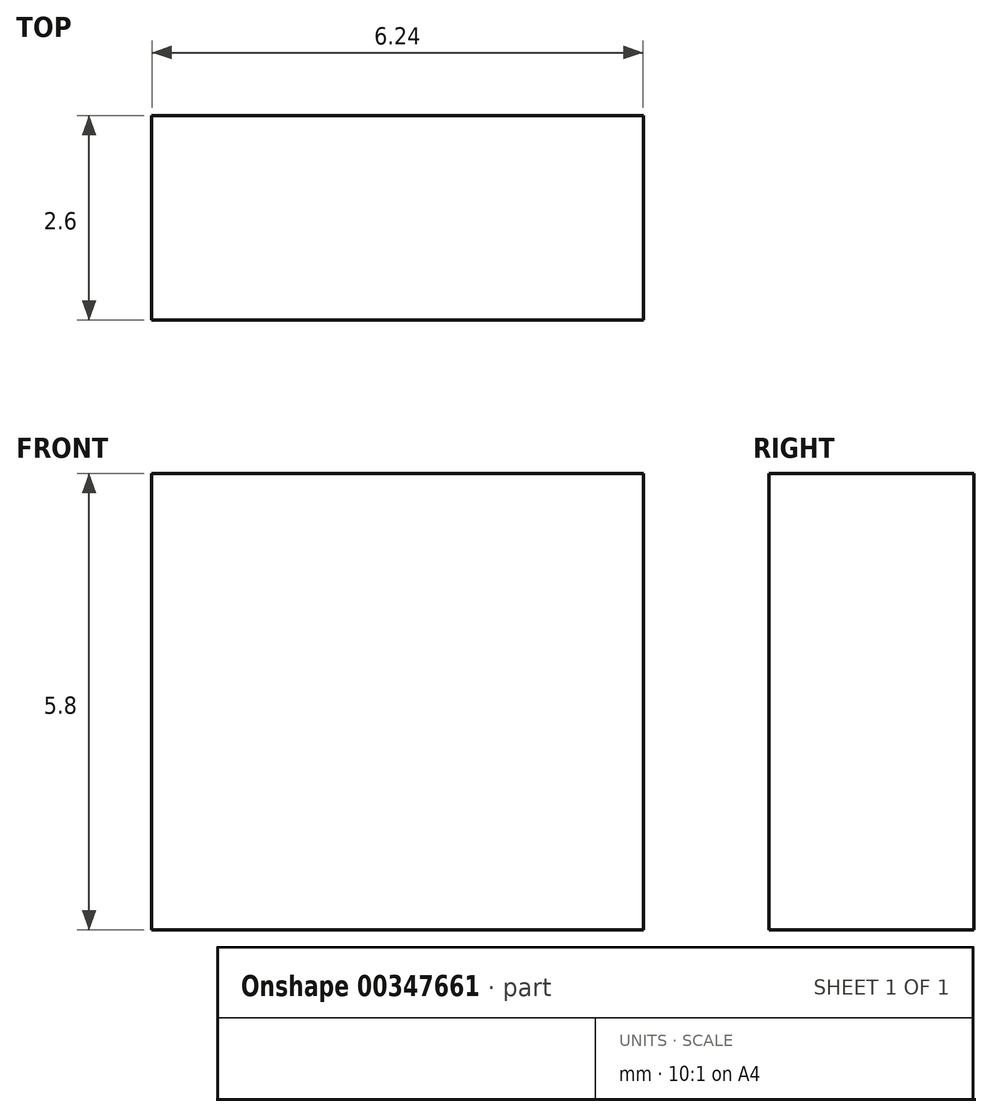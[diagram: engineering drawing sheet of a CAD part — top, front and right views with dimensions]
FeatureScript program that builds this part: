
annotation { "Feature Type Name" : "Feature", "Feature Type Description" : "" }
export const myFeature = defineFeature(function(context is Context, id is Id, definition is map)
    precondition{}
    {
        {
            var Q0;
            Q0=qCreatedBy(makeId("Front.planeOp"),FACE);
            var sketch = newSketch(context, id + "F0", { "sketchPlane" : qUnion([Q0])});
            skLineSegment(sketch, "E0.bottom", {"start": v(3.12, 2.9) * mm, "end": v(-3.12, 2.9) * mm});
            skLineSegment(sketch, "E0.top", {"start": v(3.12, -2.9) * mm, "end": v(-3.12, -2.9) * mm});
            skLineSegment(sketch, "E0.left", {"start": v(3.13, 2.9) * mm, "end": v(3.12, -2.9) * mm});
            skLineSegment(sketch, "E0.right", {"start": v(-3.12, 2.9) * mm, "end": v(-3.12, -2.9) * mm});
            skPoint(sketch, "E0.middle", {"position": v(0, 0) * mm});
            skSolve(sketch);
        }
        {
            var Q0;
            Q0=makeQuery(id+"F0.imprint","IMPRINT",FACE,{"disambiguationData":[TD([[makeQuery(id+"F0.imprint","IMPRINT",EDGE,{"derivedFrom":sQuery(id+"F0.wireOp",EDGE,"E0.bottom")}),1.0]])]});
            extrude(context, id + "F1", {"entities" : qUnion([Q0]), "depth" : 2.6 * mm});
        }
    });
